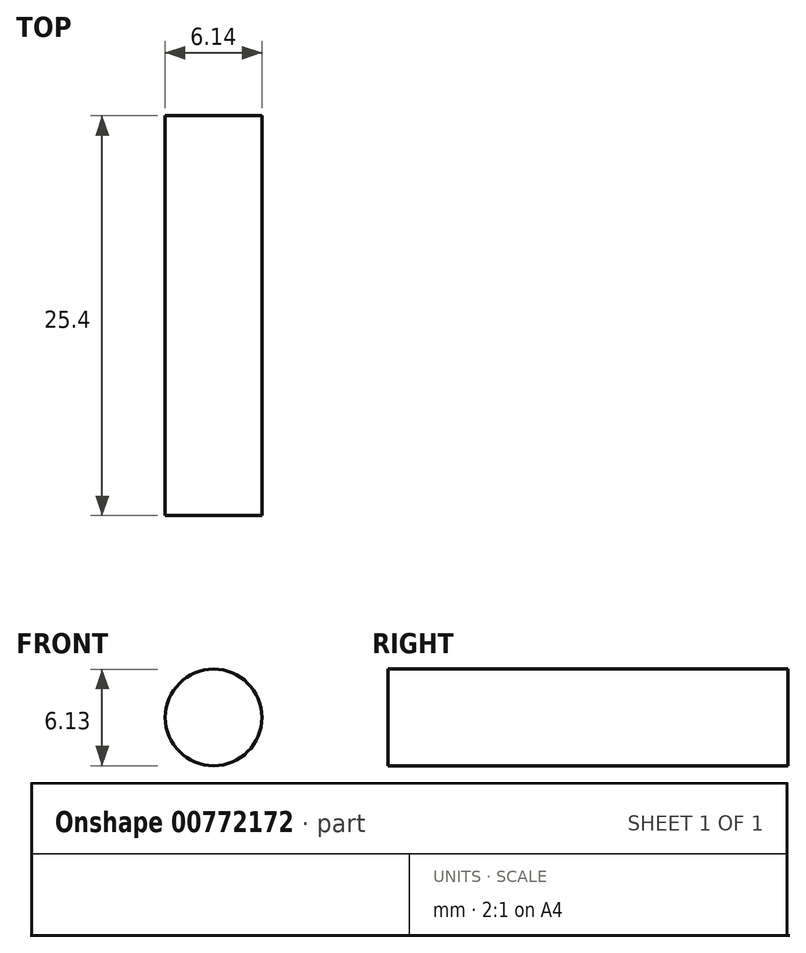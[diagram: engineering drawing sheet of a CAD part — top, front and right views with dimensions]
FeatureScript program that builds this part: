
annotation { "Feature Type Name" : "Feature", "Feature Type Description" : "" }
export const myFeature = defineFeature(function(context is Context, id is Id, definition is map)
    precondition{}
    {
        {
            var Q0;
            Q0=qCreatedBy(makeId("Front.planeOp"),FACE);
            var sketch = newSketch(context, id + "F0", { "sketchPlane" : qUnion([Q0])});
            skCircle(sketch, "E0", {"center": v(-39.55, 21.83) * mm, "radius": 3.07 * mm});
            skSolve(sketch);
        }
        {
            var Q0;
            Q0=makeQuery(id+"F0.imprint","IMPRINT",FACE,{"disambiguationData":[TD([[makeQuery(id+"F0.imprint","IMPRINT",EDGE,{"derivedFrom":sQuery(id+"F0.wireOp",EDGE,"E0")}),1.0]])]});
            extrude(context, id + "F1", {"entities" : qUnion([Q0]), "depth" : 25.4 * mm, "offsetDistance" : 25.4 * mm});
        }
    });
